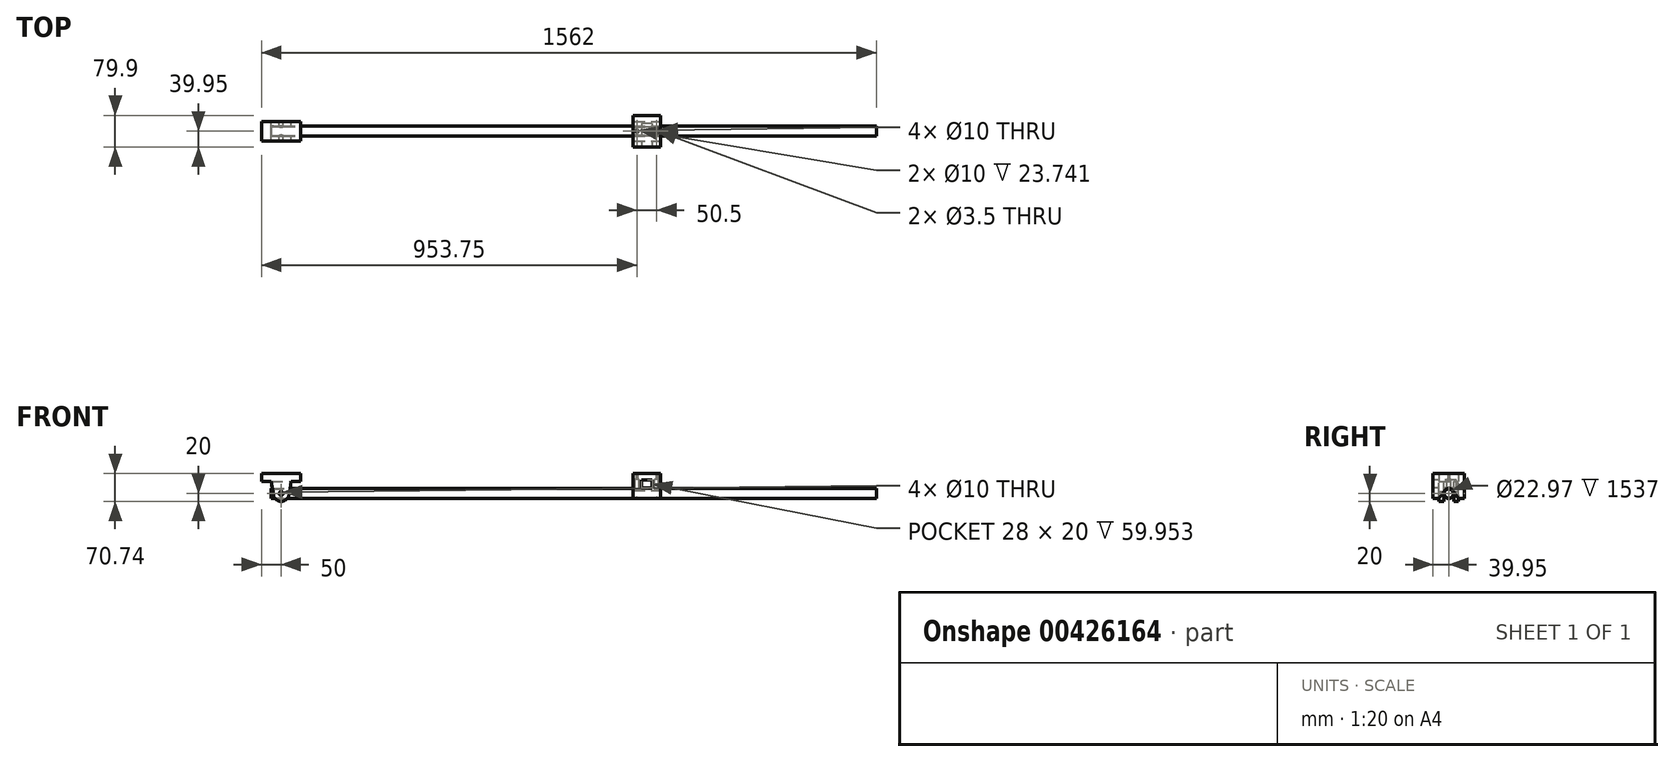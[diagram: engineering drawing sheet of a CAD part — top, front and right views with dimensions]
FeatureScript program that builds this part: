
annotation { "Feature Type Name" : "Feature", "Feature Type Description" : "" }
export const myFeature = defineFeature(function(context is Context, id is Id, definition is map)
    precondition{}
    {
        {
            var Q0;
            Q0=qCreatedBy(makeId("Front.planeOp"),FACE);
            var sketch = newSketch(context, id + "F0", { "sketchPlane" : qUnion([Q0])});
            skLineSegment(sketch, "E0.bottom", {"start": v(-50, 0) * mm, "end": v(50, 0) * mm});
            skLineSegment(sketch, "E0.top", {"start": v(-50, -20) * mm, "end": v(50, -20) * mm});
            skLineSegment(sketch, "E0.left", {"start": v(-50, 0) * mm, "end": v(-50, -20) * mm});
            skLineSegment(sketch, "E0.right", {"start": v(50, 0) * mm, "end": v(50, -20) * mm});
            skCircle(sketch, "E1", {"center": v(0, -50.74) * mm, "radius": 5 * mm});
            skArc(sketch, "E2", {"start": v(-19.7, -54.21) * mm, "mid": v(0, -70.74) * mm, "end": v(19.7, -54.21) * mm});
            skLineSegment(sketch, "E3", {"start": v(-19.7, -54.21) * mm, "end": v(-25.73, -20) * mm});
            skLineSegment(sketch, "E4", {"start": v(19.7, -54.21) * mm, "end": v(25.73, -20) * mm});
            skSolve(sketch);
        }
        {
            var Q0;
            Q0=makeQuery(id+"F0.imprint","IMPRINT",FACE,{"disambiguationData":[TD([[makeQuery(id+"F0.imprint","IMPRINT",EDGE,{"derivedFrom":sQuery(id+"F0.wireOp",EDGE,"E0.bottom")}),-1.0]])]});
            var Q1;
            Q1=makeQuery(id+"F0.imprint","IMPRINT",FACE,{"disambiguationData":[TD([[makeQuery(id+"F0.imprint","IMPRINT",EDGE,{"derivedFrom":sQuery(id+"F0.wireOp",EDGE,"E1")}),-1.0]])]});
            extrude(context, id + "F1", {"entities" : qUnion([Q0, Q1]), "endBound" : BoundingType.SYMMETRIC, "depth" : 50 * mm});
        }
        {
            var Q0;
            Q0=makeQuery(id+"F0.imprint","IMPRINT",FACE,{"disambiguationData":[TD([[makeQuery(id+"F0.imprint","IMPRINT",EDGE,{"derivedFrom":sQuery(id+"F0.wireOp",EDGE,"E1")}),-1.0]])]});
            extrude(context, id + "F2", {"entities" : qUnion([Q0]), "operationType" : NewBodyOperationType.REMOVE, "endBound" : BoundingType.SYMMETRIC, "oppositeDirection" : true, "depth" : 25 * mm});
        }
        {
            var Q0;
            Q0=qCreatedBy(makeId("Right.planeOp"),FACE);
            var sketch = newSketch(context, id + "F3", { "sketchPlane" : qUnion([Q0])});
            skCircle(sketch, "E5", {"center": v(0, -50.74) * mm, "radius": 12.5 * mm});
            skCircle(sketch, "E6", {"center": v(0, -50.74) * mm, "radius": 11.48 * mm});
            skSolve(sketch);
        }
        {
            var Q0;
            Q0=makeQuery(id+"F3.imprint","IMPRINT",FACE,{"disambiguationData":[TD([[makeQuery(id+"F3.imprint","IMPRINT",EDGE,{"derivedFrom":sQuery(id+"F3.wireOp",EDGE,"E5")}),1.0]])]});
            extrude(context, id + "F4", {"entities" : qUnion([Q0]), "operationType" : NewBodyOperationType.ADD, "oppositeDirection" : true, "depth" : 25 * mm, "hasSecondDirection" : true, "secondDirectionOppositeDirection" : false, "secondDirectionDepth" : 1512 * mm});
        }
        {
            var Q0;
            Q0=makeQuery(id+"F0.imprint","IMPRINT",FACE,{"disambiguationData":[TD([[makeQuery(id+"F0.imprint","IMPRINT",EDGE,{"derivedFrom":sQuery(id+"F0.wireOp",EDGE,"E1")}),1.0]])]});
            extrude(context, id + "F5", {"entities" : qUnion([Q0]), "operationType" : NewBodyOperationType.REMOVE, "endBound" : BoundingType.SYMMETRIC, "depth" : 62.6 * mm});
        }
        {
            var Q0;
            Q0=qCreatedBy(makeId("Right.planeOp"),FACE);
            cPlane(context, id + "F6", {"entities" : qUnion([Q0]), "cplaneType" : CPlaneType.OFFSET, "offset" : 929 * mm, "width" : 150 * mm, "height" : 150 * mm});
        }
        {
            var Q0;
            Q0=qCreatedBy(id+"F6.planeOp",FACE);
            var sketch = newSketch(context, id + "F7", { "sketchPlane" : qUnion([Q0])});
            skArc(sketch, "E7", {"start": v(10.26, -42.76) * mm, "mid": v(0, -37.74) * mm, "end": v(-10.26, -42.76) * mm});
            skLineSegment(sketch, "E8", {"start": v(0, -50.74) * mm, "end": v(0, 0) * mm, "construction": true});
            skLineSegment(sketch, "E9", {"start": v(-10.26, -42.76) * mm, "end": v(-24.95, -63.74) * mm});
            skLineSegment(sketch, "E10", {"start": v(-24.95, -63.74) * mm, "end": v(-39.95, -63.74) * mm});
            skLineSegment(sketch, "E11", {"start": v(-39.95, -63.74) * mm, "end": v(-39.95, 0) * mm});
            skLineSegment(sketch, "E12", {"start": v(-39.95, 0) * mm, "end": v(39.95, 0) * mm});
            skLineSegment(sketch, "E13.MirrorCS", {"start": v(39.95, -63.74) * mm, "end": v(39.95, 0) * mm});
            skLineSegment(sketch, "E14.MirrorCS", {"start": v(10.26, -42.76) * mm, "end": v(24.95, -63.74) * mm});
            skLineSegment(sketch, "E15.MirrorCS", {"start": v(24.95, -63.74) * mm, "end": v(39.95, -63.74) * mm});
            skSolve(sketch);
        }
        {
            var Q0;
            Q0=makeQuery(id+"F7.imprint","IMPRINT",FACE,{"disambiguationData":[TD([[makeQuery(id+"F7.imprint","IMPRINT",EDGE,{"derivedFrom":sQuery(id+"F7.wireOp",EDGE,"E7")}),-1.0]])]});
            extrude(context, id + "F8", {"entities" : qUnion([Q0]), "endBound" : BoundingType.SYMMETRIC, "oppositeDirection" : true, "depth" : 70 * mm});
        }
        {
            var Q0;
            Q0=makeQuery(id+"F8.opExtrude","SWEPT_FACE",FACE,{"disambiguationData":[OSD([sQuery(id+"F7.wireOp",EDGE,"E12")])]});
            cPlane(context, id + "F9", {"entities" : qUnion([Q0]), "cplaneType" : CPlaneType.OFFSET, "offset" : 15 * mm, "oppositeDirection" : true, "width" : 150 * mm, "height" : 150 * mm});
        }
        {
            var Q0;
            Q0=qCreatedBy(id+"F9.planeOp",FACE);
            var sketch = newSketch(context, id + "F10", { "sketchPlane" : qUnion([Q0])});
            skCircle(sketch, "E16", {"center": v(954.25, 0) * mm, "radius": 1.75 * mm});
            skCircle(sketch, "E17", {"center": v(903.75, 0) * mm, "radius": 1.75 * mm});
            skCircle(sketch, "E18", {"center": v(954.25, 0) * mm, "radius": 5 * mm});
            skCircle(sketch, "E19", {"center": v(903.75, 0) * mm, "radius": 5 * mm});
            skSolve(sketch);
        }
        {
            var Q0;
            Q0=makeQuery(id+"F10.imprint","IMPRINT",FACE,{"disambiguationData":[TD([[makeQuery(id+"F10.imprint","IMPRINT",EDGE,{"derivedFrom":sQuery(id+"F10.wireOp",EDGE,"E17")}),-1.0]])]});
            var Q1;
            Q1=makeQuery(id+"F10.imprint","IMPRINT",FACE,{"disambiguationData":[TD([[makeQuery(id+"F10.imprint","IMPRINT",EDGE,{"derivedFrom":sQuery(id+"F10.wireOp",EDGE,"E16")}),-1.0]])]});
            var Q2;
            Q2=makeQuery(id+"F10.imprint","IMPRINT",FACE,{"disambiguationData":[TD([[makeQuery(id+"F10.imprint","IMPRINT",EDGE,{"derivedFrom":sQuery(id+"F10.wireOp",EDGE,"E17")}),1.0]])]});
            var Q3;
            Q3=makeQuery(id+"F10.imprint","IMPRINT",FACE,{"disambiguationData":[TD([[makeQuery(id+"F10.imprint","IMPRINT",EDGE,{"derivedFrom":sQuery(id+"F10.wireOp",EDGE,"E16")}),1.0]])]});
            extrude(context, id + "F11", {"entities" : qUnion([Q0, Q1, Q2, Q3]), "operationType" : NewBodyOperationType.REMOVE, "oppositeDirection" : true, "depth" : 61 * mm});
        }
        {
            var Q0;
            Q0=makeQuery(id+"F10.imprint","IMPRINT",FACE,{"disambiguationData":[TD([[makeQuery(id+"F10.imprint","IMPRINT",EDGE,{"derivedFrom":sQuery(id+"F10.wireOp",EDGE,"E17")}),1.0]])]});
            var Q1;
            Q1=makeQuery(id+"F10.imprint","IMPRINT",FACE,{"disambiguationData":[TD([[makeQuery(id+"F10.imprint","IMPRINT",EDGE,{"derivedFrom":sQuery(id+"F10.wireOp",EDGE,"E16")}),1.0]])]});
            extrude(context, id + "F12", {"entities" : qUnion([Q0, Q1]), "operationType" : NewBodyOperationType.REMOVE, "endBound" : BoundingType.THROUGH_ALL, "depth" : 25 * mm});
        }
        {
            var Q0;
            Q0=qCreatedBy(makeId("Front.planeOp"),FACE);
            var sketch = newSketch(context, id + "F13", { "sketchPlane" : qUnion([Q0])});
            skLineSegment(sketch, "E20.bottom", {"start": v(943, -36.04) * mm, "end": v(915, -36.04) * mm});
            skLineSegment(sketch, "E20.top", {"start": v(943, -16.04) * mm, "end": v(915, -16.04) * mm});
            skLineSegment(sketch, "E20.left", {"start": v(943, -36.04) * mm, "end": v(943, -16.04) * mm});
            skLineSegment(sketch, "E20.right", {"start": v(915, -36.04) * mm, "end": v(915, -16.04) * mm});
            skPoint(sketch, "E20.middle", {"position": v(929, -26.04) * mm});
            skSolve(sketch);
        }
        {
            var Q0;
            Q0=makeQuery(id+"F13.imprint","IMPRINT",FACE,{"disambiguationData":[TD([[makeQuery(id+"F13.imprint","IMPRINT",EDGE,{"derivedFrom":sQuery(id+"F13.wireOp",EDGE,"E20.bottom")}),-1.0]])]});
            extrude(context, id + "F14", {"entities" : qUnion([Q0]), "operationType" : NewBodyOperationType.REMOVE, "oppositeDirection" : true, "depth" : 20 * mm, "hasSecondDirection" : true, "secondDirectionBound" : SecondDirectionBoundingType.THROUGH_ALL, "secondDirectionOppositeDirection" : false, "secondDirectionDepth" : 25 * mm});
        }
    });
